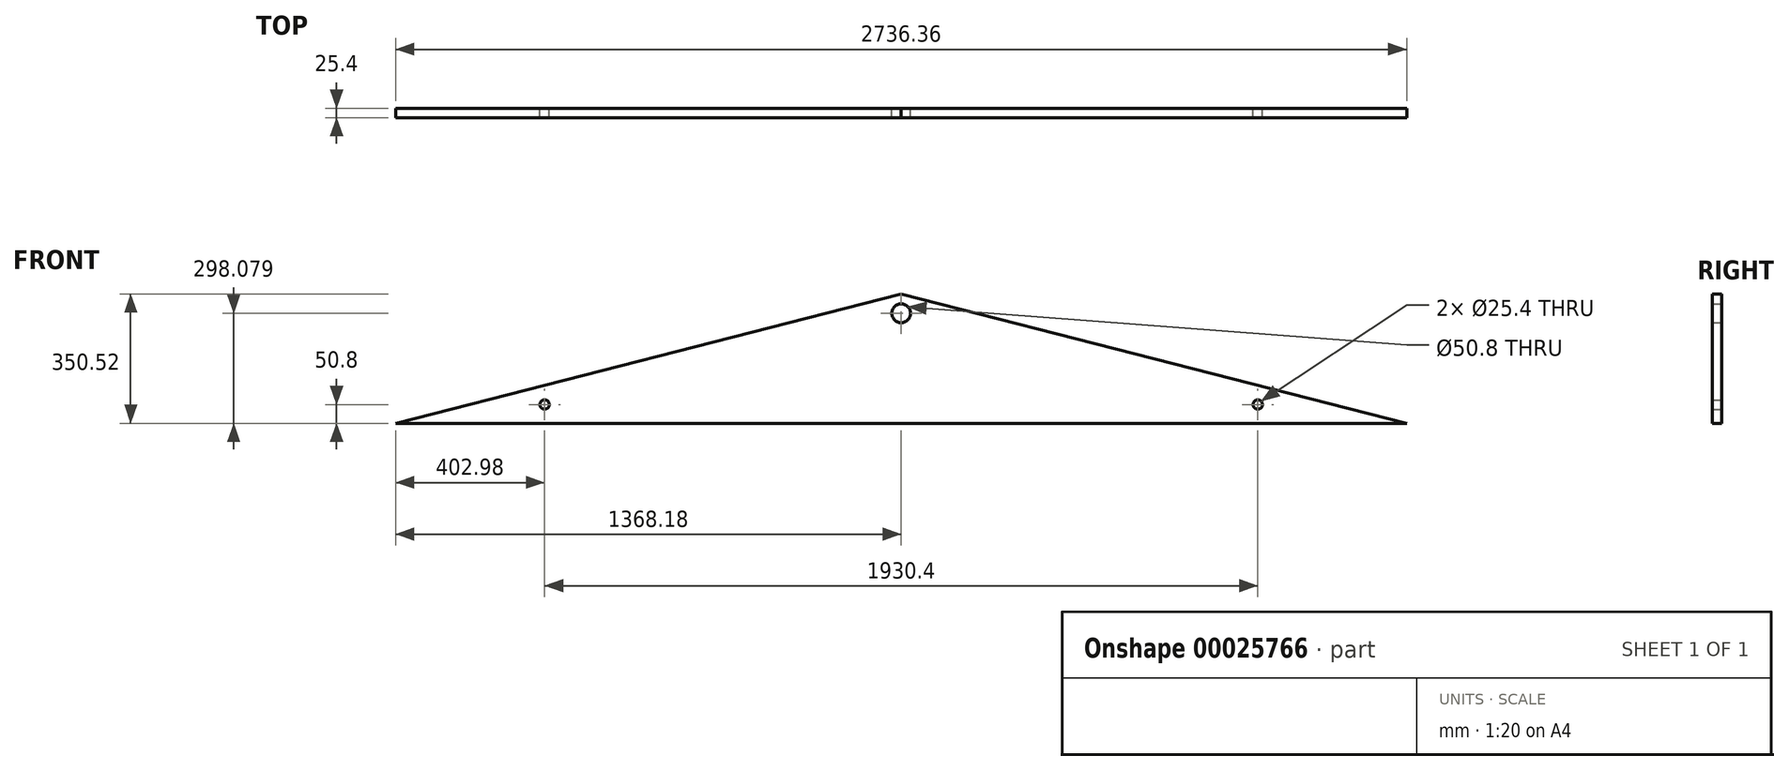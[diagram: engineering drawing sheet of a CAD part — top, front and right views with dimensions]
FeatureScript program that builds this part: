
annotation { "Feature Type Name" : "Feature", "Feature Type Description" : "" }
export const myFeature = defineFeature(function(context is Context, id is Id, definition is map)
    precondition{}
    {
        {
            var Q0;
            Q0=qCreatedBy(makeId("Front.planeOp"),FACE);
            var sketch = newSketch(context, id + "F0", { "sketchPlane" : qUnion([Q0])});
            skLineSegment(sketch, "E0", {"start": v(-1368.18, 0) * mm, "end": v(1368.18, 0) * mm});
            skLineSegment(sketch, "E1", {"start": v(1368.18, 0) * mm, "end": v(0, 350.52) * mm});
            skLineSegment(sketch, "E2", {"start": v(0, 350.52) * mm, "end": v(-1368.18, 0) * mm});
            skLineSegment(sketch, "E3.0", {"start": v(965.2, 50.8) * mm, "end": v(0, 298.08) * mm, "construction": true});
            skLineSegment(sketch, "E3.1", {"start": v(-965.2, 50.8) * mm, "end": v(965.2, 50.8) * mm, "construction": true});
            skLineSegment(sketch, "E3.2", {"start": v(0, 298.08) * mm, "end": v(-965.2, 50.8) * mm, "construction": true});
            skCircle(sketch, "E4", {"center": v(0, 298.08) * mm, "radius": 25.4 * mm});
            skCircle(sketch, "E5", {"center": v(965.2, 50.8) * mm, "radius": 12.7 * mm});
            skCircle(sketch, "E6", {"center": v(-965.2, 50.8) * mm, "radius": 12.7 * mm});
            skSolve(sketch);
        }
        {
            var Q0;
            Q0 = qSketchRegion(id + "F0", true);
            extrude(context, id + "F1", {"entities" : qUnion([Q0]), "depth" : 25.4 * mm});
        }
    });
